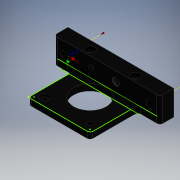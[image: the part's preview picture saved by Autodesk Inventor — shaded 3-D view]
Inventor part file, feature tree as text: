
AUTODESK INVENTOR PART (.ipt)
format: ipt  version: 2016 SP1 (Build 200210100, 210)  size: 390,656 bytes
history: native  units: mm
features: sketch x11, hole x7, extrude x3, fillet x2, plane x1, mirror x1
ambient origin geometry x8: Origin, YZ Plane, XZ Plane, XY Plane, X Axis, Y Axis, Z Axis, Center Point
bodies: Solid1 (feature_tree)
feature tree (25):
  extrude  "Extrusion1"  Depth=42.0mm
  extrude  "Extrusion2"  Depth=9.4mm
  hole  "Hole1"  [1 undecoded]
  hole  "Hole2"  [1 undecoded]
  hole  "Hole3"  [1 undecoded]
  hole  "Hole4"  [1 undecoded]
  hole  "Hole5"  [1 undecoded]
  hole  "Hole6"  [1 undecoded]
  extrude  "Extrusion3"  Depth=15.0mm
  hole  "Hole7"  [1 undecoded]
  plane  "Work Plane1"
  mirror  "Mirror1"
  fillet  "Fillet2"  Radius=10.0mm
  sketch  "Sketch11"  dims[d41=5.5mm d42=3.5mm d43=6.0mm d44=6.0mm d45=2.0mm d46=90.0deg d47=8.0mm d48=20.594885mm d49=6.5mm d50=15.0mm d51=4.917mm d52=12.0mm d53=4.0mm d54=2.0mm d55=90.0deg d56=17.1mm d57=20.594885mm d58=6.5mm d59=10.0mm d60=3.242mm d61=8.0mm d62=7.5mm d63=2.5mm d64=90.0deg d65=11.8mm d66=20.594885mm d67=1.0mm d68=15.0mm d69=0.0mm d70=5.0mm d71=8.5mm d72=17.0mm d73=7.0mm d74=5.0mm d75=6.0mm d76=4.0mm d77=2.0mm d78=90.0deg d79=8.0mm d80=20.594885mm d81=2.0mm d82=5.0mm]
  fillet  "Fillet1"  Radius=1.0mm
  sketch  "Sketch1"  dims[d0=42.0mm d1=42.0mm]
  sketch  "Sketch2"  dims[d2=4.3mm d3=0.0mm d4=9.4mm]
  sketch  "Sketch3"  dims[d5=12.7mm d6=0.0mm d7=21.0mm]
  sketch  "Sketch4"  dims[d8=21.0mm]
  sketch  "Sketch5"  dims[d9=22.3mm d10=6.0mm d11=4.0mm d12=2.0mm d13=90.0deg d14=8.0mm d15=20.594885mm d16=5.5mm]
  sketch  "Sketch6"  dims[d17=5.5mm d18=5.5mm]
  sketch  "Sketch7"  dims[d21=5.5mm]
  sketch  "Sketch8"  dims[d24=3.5mm d25=6.0mm d26=6.0mm d27=3.0mm d28=90.0deg d29=8.0mm d30=20.594885mm d31=5.5mm]
  sketch  "Sketch9"  dims[d32=5.5mm]
  sketch  "Sketch10"  dims[d33=3.5mm d34=6.0mm d35=6.0mm d36=2.0mm d37=90.0deg d38=8.0mm d39=20.594885mm d40=5.5mm]
note: 7 required parameter values undecoded (feature->parameter linkage not recoverable at this tier; creation-order binding heuristic only, values carry confidence <= 0.55)
